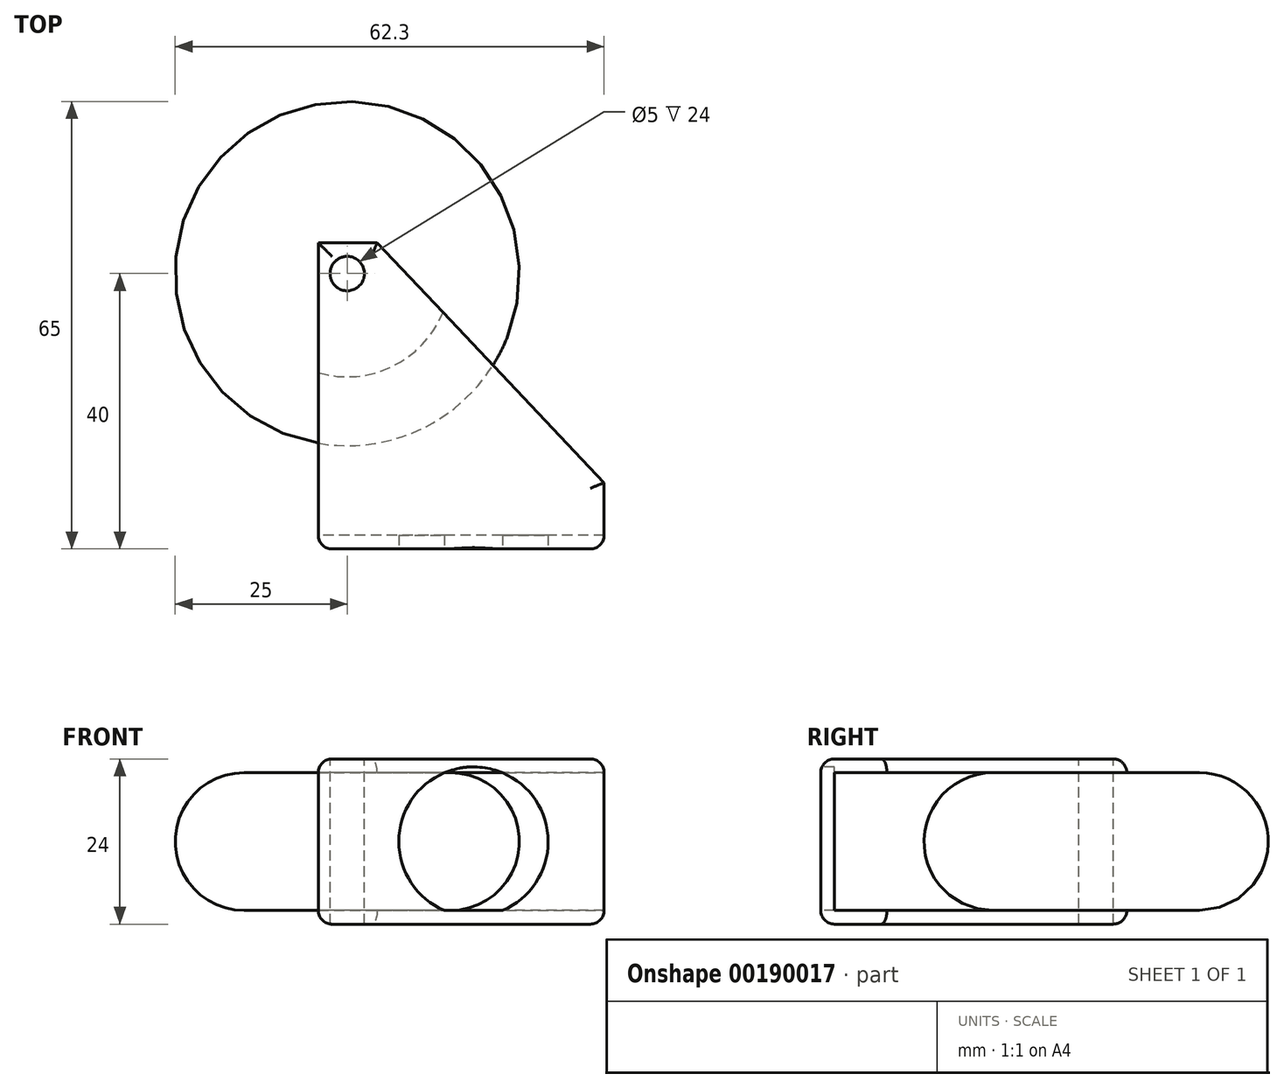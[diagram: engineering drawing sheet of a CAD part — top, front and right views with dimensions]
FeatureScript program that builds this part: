
annotation { "Feature Type Name" : "Feature", "Feature Type Description" : "" }
export const myFeature = defineFeature(function(context is Context, id is Id, definition is map)
    precondition{}
    {
        {
            var Q0;
            Q0=qCreatedBy(makeId("Top.planeOp"),FACE);
            var sketch = newSketch(context, id + "F0", { "sketchPlane" : qUnion([Q0])});
            skCircle(sketch, "E0", {"center": v(0, 0) * mm, "radius": 25 * mm});
            skSolve(sketch);
        }
        {
            var Q0;
            Q0=makeQuery(id+"F0.imprint","IMPRINT",FACE,{"disambiguationData":[TD([[makeQuery(id+"F0.imprint","IMPRINT",EDGE,{"derivedFrom":sQuery(id+"F0.wireOp",EDGE,"E0")}),1.0]])]});
            extrude(context, id + "F1", {"entities" : qUnion([Q0]), "depth" : 20 * mm});
        }
        {
            var Q0;
            Q0=makeQuery(id+"F1.opExtrude","CAP_FACE",FACE,{"disambiguationData":[OSD([sQuery(id+"F0.wireOp",EDGE,"E0")])],"isStart":false});
            var Q1;
            Q1=makeQuery(id+"F1.opExtrude","CAP_EDGE",EDGE,{"disambiguationData":[OSD([sQuery(id+"F0.wireOp",EDGE,"E0")])],"isStart":true});
            fillet(context, id + "F2", {"entities" : qUnion([Q0, Q1]), "radius" : 10 * mm, "tangentPropagation" : true, "allowEdgeOverflow" : false});
        }
        {
            var Q0;
            Q0=makeQuery(id+"F1.opExtrude","CAP_FACE",FACE,{"disambiguationData":[OSD([sQuery(id+"F0.wireOp",EDGE,"E0")])],"isStart":false});
            var sketch = newSketch(context, id + "F3", { "sketchPlane" : qUnion([Q0])});
            skCircle(sketch, "E1", {"center": v(0, 0) * mm, "radius": 2.5 * mm});
            skSolve(sketch);
        }
        {
            var Q0;
            Q0=makeQuery(id+"F3.imprint","IMPRINT",FACE,{"disambiguationData":[TD([[makeQuery(id+"F3.imprint","IMPRINT",EDGE,{"derivedFrom":sQuery(id+"F3.wireOp",EDGE,"E1")}),1.0]])]});
            extrude(context, id + "F4", {"entities" : qUnion([Q0]), "operationType" : NewBodyOperationType.REMOVE, "oppositeDirection" : true, "depth" : 25.4 * mm});
        }
        {
            var Q0;
            Q0=makeQuery(id+"F1.opExtrude","CAP_FACE",FACE,{"disambiguationData":[OSD([sQuery(id+"F0.wireOp",EDGE,"E0")])],"isStart":true});
            var sketch = newSketch(context, id + "F5", { "sketchPlane" : qUnion([Q0])});
            skLineSegment(sketch, "E2", {"start": v(37.3, 40) * mm, "end": v(37.3, 30.4) * mm});
            skLineSegment(sketch, "E3", {"start": v(-4.21, 40) * mm, "end": v(37.3, 40) * mm});
            skLineSegment(sketch, "E4", {"start": v(-4.21, 40) * mm, "end": v(-4.21, -4.46) * mm});
            skLineSegment(sketch, "E5", {"start": v(-4.21, -4.46) * mm, "end": v(4.34, -4.46) * mm});
            skLineSegment(sketch, "E6", {"start": v(4.34, -4.46) * mm, "end": v(37.3, 30.4) * mm});
            skSolve(sketch);
        }
        {
            var Q0;
            {var subQ2=sQuery(id+"F5.wireOp",EDGE,"E2");Q0=makeQuery(id+"F5.imprint","IMPRINT",FACE,{"disambiguationData":[TD([[makeQuery(id+"F5.imprint","IMPRINT",EDGE,{"derivedFrom":subQ2}),-1.0]])]});}
            var Q1;
            {var subQ0=sQuery(id+"F5.wireOp",EDGE,"E5");Q1=makeQuery(id+"F5.imprint","IMPRINT",FACE,{"disambiguationData":[TD([[makeQuery(id+"F5.imprint","IMPRINT",EDGE,{"derivedFrom":subQ0}),1.0]])]});}
            extrude(context, id + "F6", {"entities" : qUnion([Q0, Q1]), "operationType" : NewBodyOperationType.ADD, "depth" : 2 * mm});
        }
        {
            var Q0;
            Q0=makeQuery(id+"F6.opExtrude","CAP_FACE",FACE,{"disambiguationData":[OSD([sQuery(id+"F0.wireOp",EDGE,"E0"),sQuery(id+"F3.wireOp",EDGE,"E1"),sQuery(id+"F5.wireOp",EDGE,"E2"),sQuery(id+"F5.wireOp",EDGE,"E3"),sQuery(id+"F5.wireOp",EDGE,"E4"),sQuery(id+"F5.wireOp",EDGE,"E5"),sQuery(id+"F5.wireOp",EDGE,"E6")])],"isStart":true});
            var sketch = newSketch(context, id + "F7", { "sketchPlane" : qUnion([Q0])});
            skLineSegment(sketch, "E7.bottom", {"start": v(37.3, -40) * mm, "end": v(-4.21, -40) * mm});
            skLineSegment(sketch, "E7.top", {"start": v(37.3, -38) * mm, "end": v(-4.21, -38) * mm});
            skLineSegment(sketch, "E7.left", {"start": v(37.3, -40) * mm, "end": v(37.3, -38) * mm});
            skLineSegment(sketch, "E7.right", {"start": v(-4.21, -40) * mm, "end": v(-4.21, -38) * mm});
            skSolve(sketch);
        }
        {
            var Q0;
            Q0=makeQuery(id+"F7.imprint","IMPRINT",FACE,{"disambiguationData":[TD([[makeQuery(id+"F7.imprint","IMPRINT",EDGE,{"derivedFrom":sQuery(id+"F7.wireOp",EDGE,"E7.bottom")}),1.0]])]});
            extrude(context, id + "F8", {"entities" : qUnion([Q0]), "operationType" : NewBodyOperationType.ADD, "depth" : 20 * mm});
        }
        {
            var Q0;
            Q0=makeQuery(id+"F8.opExtrude","CAP_FACE",FACE,{"disambiguationData":[OSD([sQuery(id+"F7.wireOp",EDGE,"E7.bottom"),sQuery(id+"F7.wireOp",EDGE,"E7.top"),sQuery(id+"F7.wireOp",EDGE,"E7.left"),sQuery(id+"F7.wireOp",EDGE,"E7.right")])],"isStart":false});
            var sketch = newSketch(context, id + "F9", { "sketchPlane" : qUnion([Q0])});
            skLineSegment(sketch, "E8.0.0", {"start": v(37.3, -30.4) * mm, "end": v(37.3, -40) * mm});
            skLineSegment(sketch, "E8.0.1", {"start": v(37.3, -40) * mm, "end": v(-4.21, -40) * mm});
            skLineSegment(sketch, "E8.0.2", {"start": v(-4.21, -40) * mm, "end": v(-4.21, 4.46) * mm});
            skLineSegment(sketch, "E8.0.3", {"start": v(-4.21, 4.46) * mm, "end": v(4.34, 4.46) * mm});
            skLineSegment(sketch, "E8.0.4", {"start": v(4.34, 4.46) * mm, "end": v(37.3, -30.4) * mm});
            skCircle(sketch, "E9.0", {"center": v(0, 0) * mm, "radius": 2.5 * mm});
            skSolve(sketch);
        }
        {
            var Q0;
            {var subQ3=sQuery(id+"F9.wireOp",EDGE,"E8.0.3");Q0=makeQuery(id+"F9.imprint","IMPRINT",FACE,{"disambiguationData":[TD([[makeQuery(id+"F9.imprint","IMPRINT",EDGE,{"derivedFrom":subQ3}),-1.0]])]});}
            var Q1;
            {var subQ0=sQuery(id+"F9.wireOp",EDGE,"E8.0.1");Q1=makeQuery(id+"F9.imprint","IMPRINT",FACE,{"disambiguationData":[TD([[makeQuery(id+"F9.imprint","IMPRINT",EDGE,{"derivedFrom":subQ0}),1.0]])]});}
            extrude(context, id + "F10", {"entities" : qUnion([Q0, Q1]), "operationType" : NewBodyOperationType.ADD, "depth" : 2 * mm});
        }
        {
            var Q0;
            Q0=makeQuery(id+"F10.boolean.opBoolean","MERGE",EDGE,{"derivedFrom":[makeQuery(id+"F8.boolean.opBoolean","MERGE",EDGE,{"derivedFrom":[makeQuery(id+"F6.opExtrude","SWEPT_EDGE",EDGE,{"disambiguationData":[OSD([sQuery(id+"F5.wireOp",EDGE,"E3"),sQuery(id+"F5.wireOp",EDGE,"E4")])]}),makeQuery(id+"F8.opExtrude","SWEPT_EDGE",EDGE,{"disambiguationData":[OSD([sQuery(id+"F7.wireOp",EDGE,"E7.bottom"),sQuery(id+"F7.wireOp",EDGE,"E7.right")])]})]}),makeQuery(id+"F10.opExtrude","SWEPT_EDGE",EDGE,{"disambiguationData":[OSD([sQuery(id+"F9.wireOp",EDGE,"E8.0.1"),sQuery(id+"F9.wireOp",EDGE,"E8.0.2")])]})]});
            var Q1;
            Q1=makeQuery(id+"F10.opExtrude","CAP_EDGE",EDGE,{"disambiguationData":[OSD([sQuery(id+"F9.wireOp",EDGE,"E8.0.2")])],"isStart":false});
            var Q2;
            Q2=makeQuery(id+"F6.opExtrude","CAP_EDGE",EDGE,{"disambiguationData":[OSD([sQuery(id+"F5.wireOp",EDGE,"E4")])],"isStart":false});
            var Q3;
            Q3=makeQuery(id+"F10.opExtrude","CAP_EDGE",EDGE,{"disambiguationData":[OSD([sQuery(id+"F9.wireOp",EDGE,"E8.0.1")])],"isStart":false});
            var Q4;
            Q4=makeQuery(id+"F6.opExtrude","CAP_EDGE",EDGE,{"disambiguationData":[OSD([sQuery(id+"F5.wireOp",EDGE,"E3")])],"isStart":false});
            var Q5;
            Q5=makeQuery(id+"F10.boolean.opBoolean","MERGE",EDGE,{"derivedFrom":[makeQuery(id+"F8.boolean.opBoolean","MERGE",EDGE,{"derivedFrom":[makeQuery(id+"F6.opExtrude","SWEPT_EDGE",EDGE,{"disambiguationData":[OSD([sQuery(id+"F5.wireOp",EDGE,"E2"),sQuery(id+"F5.wireOp",EDGE,"E3")])]}),makeQuery(id+"F8.opExtrude","SWEPT_EDGE",EDGE,{"disambiguationData":[OSD([sQuery(id+"F7.wireOp",EDGE,"E7.bottom"),sQuery(id+"F7.wireOp",EDGE,"E7.left")])]})]}),makeQuery(id+"F10.opExtrude","SWEPT_EDGE",EDGE,{"disambiguationData":[OSD([sQuery(id+"F9.wireOp",EDGE,"E8.0.0"),sQuery(id+"F9.wireOp",EDGE,"E8.0.1")])]})]});
            var Q6;
            Q6=makeQuery(id+"F10.opExtrude","CAP_EDGE",EDGE,{"disambiguationData":[OSD([sQuery(id+"F9.wireOp",EDGE,"E8.0.0")])],"isStart":false});
            var Q7;
            Q7=makeQuery(id+"F10.opExtrude","CAP_EDGE",EDGE,{"disambiguationData":[OSD([sQuery(id+"F9.wireOp",EDGE,"E8.0.4")])],"isStart":false});
            var Q8;
            Q8=makeQuery(id+"F10.opExtrude","CAP_EDGE",EDGE,{"disambiguationData":[OSD([sQuery(id+"F9.wireOp",EDGE,"E8.0.3")])],"isStart":false});
            var Q9;
            Q9=makeQuery(id+"F6.opExtrude","CAP_EDGE",EDGE,{"disambiguationData":[OSD([sQuery(id+"F5.wireOp",EDGE,"E2")])],"isStart":false});
            var Q10;
            Q10=makeQuery(id+"F6.opExtrude","CAP_EDGE",EDGE,{"disambiguationData":[OSD([sQuery(id+"F5.wireOp",EDGE,"E6")])],"isStart":false});
            var Q11;
            Q11=makeQuery(id+"F6.opExtrude","CAP_EDGE",EDGE,{"disambiguationData":[OSD([sQuery(id+"F5.wireOp",EDGE,"E5")])],"isStart":false});
            fillet(context, id + "F11", {"entities" : qUnion([Q0, Q1, Q2, Q3, Q4, Q5, Q6, Q7, Q8, Q9, Q10, Q11]), "radius" : 2 * mm, "tangentPropagation" : true, "allowEdgeOverflow" : false});
        }
        {
            var Q0;
            Q0=makeQuery(id+"F10.boolean.opBoolean","MERGE",FACE,{"derivedFrom":[makeQuery(id+"F8.boolean.opBoolean","MERGE",FACE,{"derivedFrom":[makeQuery(id+"F6.opExtrude","SWEPT_FACE",FACE,{"disambiguationData":[OSD([sQuery(id+"F5.wireOp",EDGE,"E3")])]}),makeQuery(id+"F8.opExtrude","SWEPT_FACE",FACE,{"disambiguationData":[OSD([sQuery(id+"F7.wireOp",EDGE,"E7.bottom")])]})]}),makeQuery(id+"F10.opExtrude","SWEPT_FACE",FACE,{"disambiguationData":[OSD([sQuery(id+"F9.wireOp",EDGE,"E8.0.1")])]})]});
            var sketch = newSketch(context, id + "F12", { "sketchPlane" : qUnion([Q0])});
            skCircle(sketch, "E10", {"center": v(18.33, 10) * mm, "radius": 10.85 * mm});
            skSolve(sketch);
        }
        {
            var Q0;
            {var subQ0=sQuery(id+"F12.wireOp",EDGE,"E10");var subQ1=sQuery(id+"F9.wireOp",EDGE,"E8.0.1");var subQ2=sQuery(id+"F5.wireOp",EDGE,"E3");var subQ3=makeQuery(id+"F10.boolean.opBoolean","MERGE",FACE,{"derivedFrom":[makeQuery(id+"F8.boolean.opBoolean","MERGE",FACE,{"derivedFrom":[makeQuery(id+"F6.opExtrude","SWEPT_FACE",FACE,{"disambiguationData":[OSD([subQ2])]}),makeQuery(id+"F8.opExtrude","SWEPT_FACE",FACE,{"disambiguationData":[OSD([sQuery(id+"F7.wireOp",EDGE,"E7.bottom")])]})]}),makeQuery(id+"F10.opExtrude","SWEPT_FACE",FACE,{"disambiguationData":[OSD([subQ1])]})]});var subQ4=makeQuery(id+"F11.opFillet","BLEND_EDGE",EDGE,{"blendedFrom":[makeQuery(id+"F10.opExtrude","CAP_EDGE",EDGE,{"disambiguationData":[OSD([subQ1])],"isStart":false}),subQ3],"blendedInto":[subQ3]});var subQ5=makeQuery(id+"F12.imprint","INTERSECT",VERTEX,{"disambiguationData":[OD(0.0)],"derivedFrom":[subQ4,subQ0]});Q0=makeQuery(id+"F12.imprint","IMPRINT",FACE,{"disambiguationData":[TD([[makeQuery(id+"F12.imprint","IMPRINT",EDGE,{"disambiguationData":[TD([[subQ5,-1.0]])],"derivedFrom":subQ0}),1.0]])]});}
            var Q1;
            {var subQ0=sQuery(id+"F12.wireOp",EDGE,"E10");var subQ1=sQuery(id+"F9.wireOp",EDGE,"E8.0.1");var subQ2=makeQuery(id+"F11.opFillet","BLEND_EDGE",EDGE,{"blendedFrom":[makeQuery(id+"F10.opExtrude","CAP_EDGE",EDGE,{"disambiguationData":[OSD([subQ1])],"isStart":false}),makeQuery(id+"F10.boolean.opBoolean","MERGE",FACE,{"derivedFrom":[makeQuery(id+"F8.boolean.opBoolean","MERGE",FACE,{"derivedFrom":[makeQuery(id+"F6.opExtrude","SWEPT_FACE",FACE,{"disambiguationData":[OSD([sQuery(id+"F5.wireOp",EDGE,"E3")])]}),makeQuery(id+"F8.opExtrude","SWEPT_FACE",FACE,{"disambiguationData":[OSD([sQuery(id+"F7.wireOp",EDGE,"E7.bottom")])]})]}),makeQuery(id+"F10.opExtrude","SWEPT_FACE",FACE,{"disambiguationData":[OSD([subQ1])]})]})],"blendedInto":[makeQuery(id+"F10.boolean.opBoolean","MERGE",FACE,{"derivedFrom":[makeQuery(id+"F8.boolean.opBoolean","MERGE",FACE,{"derivedFrom":[makeQuery(id+"F6.opExtrude","SWEPT_FACE",FACE,{"disambiguationData":[OSD([sQuery(id+"F5.wireOp",EDGE,"E3")])]}),makeQuery(id+"F8.opExtrude","SWEPT_FACE",FACE,{"disambiguationData":[OSD([sQuery(id+"F7.wireOp",EDGE,"E7.bottom")])]})]}),makeQuery(id+"F10.opExtrude","SWEPT_FACE",FACE,{"disambiguationData":[OSD([subQ1])]})]})]});var subQ3=makeQuery(id+"F12.imprint","INTERSECT",VERTEX,{"disambiguationData":[OD(0.0)],"derivedFrom":[subQ2,subQ0]});Q1=makeQuery(id+"F12.imprint","IMPRINT",FACE,{"disambiguationData":[TD([[makeQuery(id+"F12.imprint","IMPRINT",EDGE,{"disambiguationData":[TD([[subQ3,1.0]])],"derivedFrom":subQ0}),1.0]])]});}
            var Q2;
            {var subQ0=sQuery(id+"F12.wireOp",EDGE,"E10");var subQ1=sQuery(id+"F5.wireOp",EDGE,"E3");var subQ2=makeQuery(id+"F11.opFillet","BLEND_EDGE",EDGE,{"blendedFrom":[makeQuery(id+"F6.opExtrude","CAP_EDGE",EDGE,{"disambiguationData":[OSD([subQ1])],"isStart":false}),makeQuery(id+"F10.boolean.opBoolean","MERGE",FACE,{"derivedFrom":[makeQuery(id+"F8.boolean.opBoolean","MERGE",FACE,{"derivedFrom":[makeQuery(id+"F6.opExtrude","SWEPT_FACE",FACE,{"disambiguationData":[OSD([subQ1])]}),makeQuery(id+"F8.opExtrude","SWEPT_FACE",FACE,{"disambiguationData":[OSD([sQuery(id+"F7.wireOp",EDGE,"E7.bottom")])]})]}),makeQuery(id+"F10.opExtrude","SWEPT_FACE",FACE,{"disambiguationData":[OSD([sQuery(id+"F9.wireOp",EDGE,"E8.0.1")])]})]})],"blendedInto":[makeQuery(id+"F10.boolean.opBoolean","MERGE",FACE,{"derivedFrom":[makeQuery(id+"F8.boolean.opBoolean","MERGE",FACE,{"derivedFrom":[makeQuery(id+"F6.opExtrude","SWEPT_FACE",FACE,{"disambiguationData":[OSD([subQ1])]}),makeQuery(id+"F8.opExtrude","SWEPT_FACE",FACE,{"disambiguationData":[OSD([sQuery(id+"F7.wireOp",EDGE,"E7.bottom")])]})]}),makeQuery(id+"F10.opExtrude","SWEPT_FACE",FACE,{"disambiguationData":[OSD([sQuery(id+"F9.wireOp",EDGE,"E8.0.1")])]})]})]});var subQ3=makeQuery(id+"F12.imprint","INTERSECT",VERTEX,{"disambiguationData":[OD(0.0)],"derivedFrom":[subQ2,subQ0]});Q2=makeQuery(id+"F12.imprint","IMPRINT",FACE,{"disambiguationData":[TD([[makeQuery(id+"F12.imprint","IMPRINT",EDGE,{"disambiguationData":[TD([[subQ3,-1.0]])],"derivedFrom":subQ0}),1.0]])]});}
            extrude(context, id + "F13", {"entities" : qUnion([Q0, Q1, Q2]), "operationType" : NewBodyOperationType.REMOVE, "oppositeDirection" : true, "depth" : 2 * mm});
        }
    });
